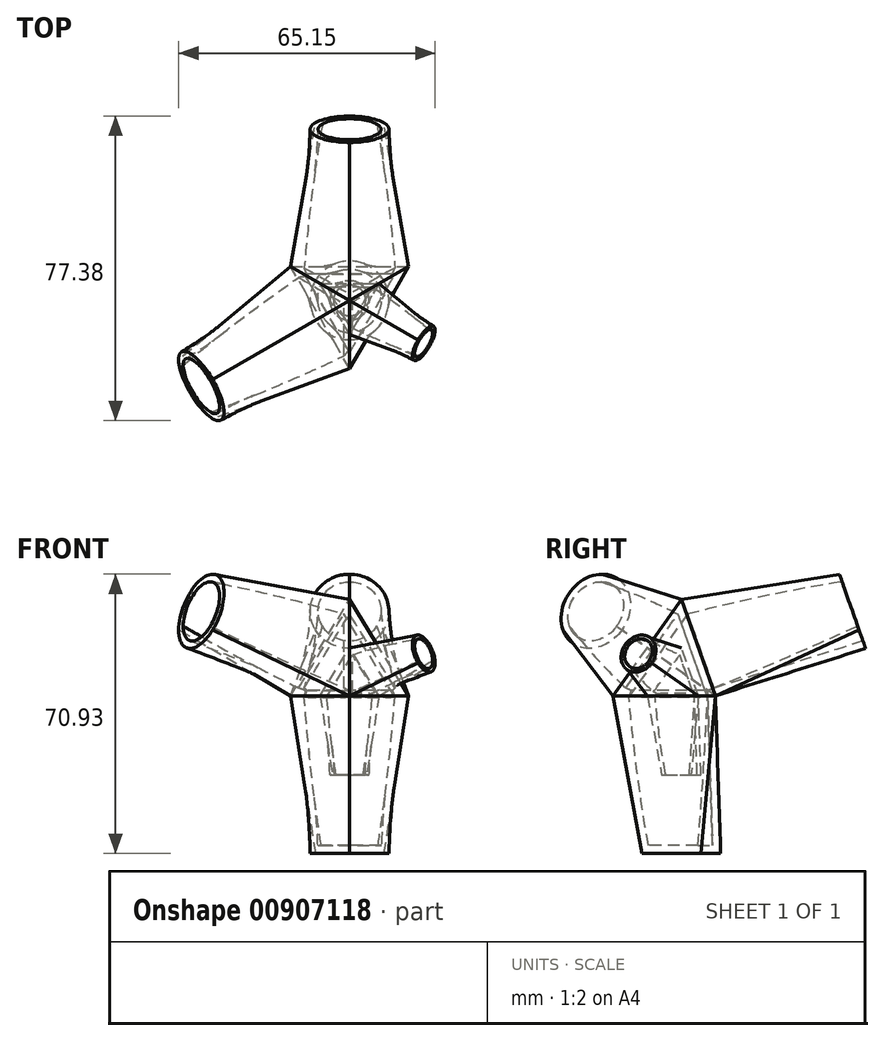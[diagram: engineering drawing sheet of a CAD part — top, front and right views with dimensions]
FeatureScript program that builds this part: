
annotation { "Feature Type Name" : "Feature", "Feature Type Description" : "" }
export const myFeature = defineFeature(function(context is Context, id is Id, definition is map)
    precondition{}
    {
        {
            var Q0;
            Q0=qCreatedBy(makeId("Top.planeOp"),FACE);
            var sketch = newSketch(context, id + "F0", { "sketchPlane" : qUnion([Q0])});
            skLineSegment(sketch, "E0.0", {"start": v(-15, 8.66) * mm, "end": v(15, 8.66) * mm});
            skLineSegment(sketch, "E0.1", {"start": v(15, 8.66) * mm, "end": v(0, -17.32) * mm});
            skLineSegment(sketch, "E0.2", {"start": v(0, -17.32) * mm, "end": v(-15, 8.66) * mm});
            skCircle(sketch, "E1", {"center": v(0, 0) * mm, "radius": 17.32 * mm, "construction": true});
            skSolve(sketch);
        }
        {
            var Q0;
            Q0=qCreatedBy(makeId("Right.planeOp"),FACE);
            var sketch = newSketch(context, id + "F1", { "sketchPlane" : qUnion([Q0])});
            skLineSegment(sketch, "E2", {"start": v(0, 0) * mm, "end": v(0, 24.5) * mm, "construction": true});
            skLineSegment(sketch, "E3", {"start": v(0, 24.5) * mm, "end": v(-17.32, 0) * mm, "construction": true});
            skSolve(sketch);
        }
        {
            var Q0;
            Q0=qCreatedBy(makeId("Top.planeOp"),FACE);
            var Q1;
            Q1=sQuery(id+"F1.wireOp",VERTEX,"E2.end");
            cPlane(context, id + "F2", {"entities" : qUnion([Q0, Q1]), "cplaneType" : CPlaneType.PLANE_POINT, "offset" : 25 * mm, "width" : 150 * mm, "height" : 150 * mm});
        }
        {
            var Q0;
            Q0=qCreatedBy(id+"F2.planeOp",FACE);
            var sketch = newSketch(context, id + "F3", { "sketchPlane" : qUnion([Q0])});
            skPoint(sketch, "E4", {"position": v(0, 0) * mm});
            skSolve(sketch);
        }
        {
            var Q0;
            Q0=makeQuery(id+"F0.imprint","IMPRINT",FACE,{"disambiguationData":[TD([[makeQuery(id+"F0.imprint","IMPRINT",EDGE,{"derivedFrom":sQuery(id+"F0.wireOp",EDGE,"E0.0")}),-1.0]])]});
            var Q1;
            Q1=sQuery(id+"F3.wireOp",VERTEX,"E4");
            loft(context, id + "F4", {"sheetProfilesArray" : [{ "sheetProfileEntities" : qUnion([Q0]) }, { "sheetProfileEntities" : qUnion([Q1]) }]});
        }
        {
            var Q0;
            Q0=makeQuery(id+"F4.opLoft","CAP_FACE",FACE,{"disambiguationData":[OSD([makeQuery(id+"F0.imprint","IMPRINT",FACE,{"disambiguationData":[TD([[makeQuery(id+"F0.imprint","IMPRINT",EDGE,{"derivedFrom":sQuery(id+"F0.wireOp",EDGE,"E0.0")}),-1.0]])]})])],"isStart":true});
            cPlane(context, id + "F5", {"entities" : qUnion([Q0]), "cplaneType" : CPlaneType.OFFSET, "offset" : 40 * mm, "width" : 150 * mm, "height" : 150 * mm});
        }
        {
            var Q0;
            Q0=qCreatedBy(id+"F5.planeOp",FACE);
            var sketch = newSketch(context, id + "F6", { "sketchPlane" : qUnion([Q0])});
            skPoint(sketch, "E5", {"position": v(0, 0) * mm});
            skCircle(sketch, "E6", {"center": v(0, 0) * mm, "radius": 10 * mm});
            skSolve(sketch);
        }
        {
            var Q1;
            Q1=makeQuery(id+"F4.opLoft","CAP_FACE",FACE,{"disambiguationData":[OSD([makeQuery(id+"F0.imprint","IMPRINT",FACE,{"disambiguationData":[TD([[makeQuery(id+"F0.imprint","IMPRINT",EDGE,{"derivedFrom":sQuery(id+"F0.wireOp",EDGE,"E0.0")}),-1.0]])]})])],"isStart":true});
            var Q2;
            Q2=makeQuery(id+"F6.imprint","IMPRINT",FACE,{"disambiguationData":[TD([[makeQuery(id+"F6.imprint","IMPRINT",EDGE,{"derivedFrom":sQuery(id+"F6.wireOp",EDGE,"E6")}),1.0]])]});
            loft(context, id + "F7", {"operationType" : NewBodyOperationType.ADD, "sheetProfilesArray" : [{ "sheetProfileEntities" : qUnion([Q1]) }, { "sheetProfileEntities" : qUnion([Q2]) }]});
        }
        {
            var Q0;
            {var subQ0=sQuery(id+"F0.wireOp",EDGE,"E0.1");var subQ1=sQuery(id+"F0.wireOp",EDGE,"E0.2");var subQ2=sQuery(id+"F0.wireOp",EDGE,"E0.0");Q0=makeQuery(id+"F4.opLoft","SWEPT_FACE",FACE,{"disambiguationData":[OSD([subQ2,subQ0,subQ1]),TDD([makeQuery(id+"F0.imprint","INTERSECT",VERTEX,{"derivedFrom":[subQ2,subQ0]}),makeQuery(id+"F0.imprint","INTERSECT",VERTEX,{"derivedFrom":[subQ0,subQ1]}),makeQuery(id+"F0.imprint","IMPRINT",EDGE,{"derivedFrom":subQ0})])]});}
            cPlane(context, id + "F8", {"entities" : qUnion([Q0]), "cplaneType" : CPlaneType.OFFSET, "offset" : 40 * mm, "width" : 150 * mm, "height" : 150 * mm});
        }
        {
            var Q0;
            Q0=qCreatedBy(id+"F8.planeOp",FACE);
            var sketch = newSketch(context, id + "F9", { "sketchPlane" : qUnion([Q0])});
            skPoint(sketch, "E7", {"position": v(1.1, 5.67) * mm});
            skLineSegment(sketch, "E8", {"start": v(1.1, 5.67) * mm, "end": v(-15.28, 0) * mm, "construction": true});
            skLineSegment(sketch, "E9", {"start": v(1.1, 5.67) * mm, "end": v(4.36, 22.68) * mm, "construction": true});
            skLineSegment(sketch, "E10", {"start": v(1.1, 5.67) * mm, "end": v(14.18, -5.67) * mm, "construction": true});
            skCircle(sketch, "E11", {"center": v(1.1, 5.67) * mm, "radius": 10 * mm});
            skSolve(sketch);
        }
        {
            var Q0;
            Q0=qCreatedBy(makeId("Top.planeOp"),FACE);
            var sketch = newSketch(context, id + "F10", { "sketchPlane" : qUnion([Q0])});
            skCircle(sketch, "E12", {"center": v(0, 0) * mm, "radius": 23.5 * mm, "construction": true});
            skSolve(sketch);
        }
        {
            var Q1;
            {var subQ0=sQuery(id+"F0.wireOp",EDGE,"E0.1");var subQ1=sQuery(id+"F0.wireOp",EDGE,"E0.2");var subQ2=sQuery(id+"F0.wireOp",EDGE,"E0.0");Q1=makeQuery(id+"F4.opLoft","SWEPT_FACE",FACE,{"disambiguationData":[OSD([subQ2,subQ0,subQ1]),TDD([makeQuery(id+"F0.imprint","INTERSECT",VERTEX,{"derivedFrom":[subQ2,subQ0]}),makeQuery(id+"F0.imprint","INTERSECT",VERTEX,{"derivedFrom":[subQ0,subQ1]}),makeQuery(id+"F0.imprint","IMPRINT",EDGE,{"derivedFrom":subQ0})])]});}
            var Q2;
            Q2=makeQuery(id+"F9.imprint","IMPRINT",FACE,{"disambiguationData":[TD([[makeQuery(id+"F9.imprint","IMPRINT",EDGE,{"derivedFrom":sQuery(id+"F9.wireOp",EDGE,"E11")}),1.0]])]});
            loft(context, id + "F11", {"operationType" : NewBodyOperationType.ADD, "sheetProfilesArray" : [{ "sheetProfileEntities" : qUnion([Q1]) }, { "sheetProfileEntities" : qUnion([Q2]) }]});
        }
        {
            var Q0;
            Q0=makeQuery(id+"F4.opLoft","SWEPT_BODY",BODY,{"disambiguationData":[OSD([makeQuery(id+"F0.imprint","IMPRINT",FACE,{"disambiguationData":[TD([[makeQuery(id+"F0.imprint","IMPRINT",EDGE,{"derivedFrom":sQuery(id+"F0.wireOp",EDGE,"E0.0")}),-1.0]])]}),sQuery(id+"F3.wireOp",VERTEX,"E4")])]});
            var Q1;
            Q1=sQuery(id+"F10.wireOp",EDGE,"E12");
            circularPattern(context, id + "F12", {"entities" : qUnion([Q0]), "axis" : qUnion([Q1]), "angle" : 360 * degree, "instanceCount" : 3, "equalSpace" : true});
        }
        {
            var Q0;
            Q0=makeQuery(id+"F12.opPattern","COPY",FACE,{"derivedFrom":makeQuery(id+"F11.opLoft","CAP_FACE",FACE,{"disambiguationData":[OSD([makeQuery(id+"F9.imprint","IMPRINT",FACE,{"disambiguationData":[TD([[makeQuery(id+"F9.imprint","IMPRINT",EDGE,{"derivedFrom":sQuery(id+"F9.wireOp",EDGE,"E11")}),1.0]])]})])],"isStart":true}),"instanceName":"1"});
            var Q1;
            Q1=makeQuery(id+"F7.opLoft","CAP_FACE",FACE,{"disambiguationData":[OSD([makeQuery(id+"F6.imprint","IMPRINT",FACE,{"disambiguationData":[TD([[makeQuery(id+"F6.imprint","IMPRINT",EDGE,{"derivedFrom":sQuery(id+"F6.wireOp",EDGE,"E6")}),1.0]])]})])],"isStart":true});
            var Q2;
            Q2=makeQuery(id+"F12.opPattern","COPY",FACE,{"derivedFrom":makeQuery(id+"F11.opLoft","CAP_FACE",FACE,{"disambiguationData":[OSD([makeQuery(id+"F9.imprint","IMPRINT",FACE,{"disambiguationData":[TD([[makeQuery(id+"F9.imprint","IMPRINT",EDGE,{"derivedFrom":sQuery(id+"F9.wireOp",EDGE,"E11")}),1.0]])]})])],"isStart":true}),"instanceName":"2"});
            var Q3;
            Q3=makeQuery(id+"F11.opLoft","CAP_FACE",FACE,{"disambiguationData":[OSD([makeQuery(id+"F9.imprint","IMPRINT",FACE,{"disambiguationData":[TD([[makeQuery(id+"F9.imprint","IMPRINT",EDGE,{"derivedFrom":sQuery(id+"F9.wireOp",EDGE,"E11")}),1.0]])]})])],"isStart":true});
            shell(context, id + "F13", {"entities" : qUnion([Q0, Q1, Q2, Q3]), "thickness" : 2 * mm});
        }
        {
            var Q0;
            Q0=makeQuery(id+"F4.opLoft","SWEPT_BODY",BODY,{"disambiguationData":[OSD([makeQuery(id+"F0.imprint","IMPRINT",FACE,{"disambiguationData":[TD([[makeQuery(id+"F0.imprint","IMPRINT",EDGE,{"derivedFrom":sQuery(id+"F0.wireOp",EDGE,"E0.0")}),-1.0]])]}),sQuery(id+"F3.wireOp",VERTEX,"E4")])]});
            var Q1;
            Q1=qCreatedBy(makeId("Origin.pointOp"),VERTEX);
            transform(context, id + "F14", {"entities" : qUnion([Q0]), "transformType" : TransformType.SCALE_UNIFORMLY, "scale" : .5, "scalePoint" : qUnion([Q1]), "makeCopy" : false});
        }
    });
